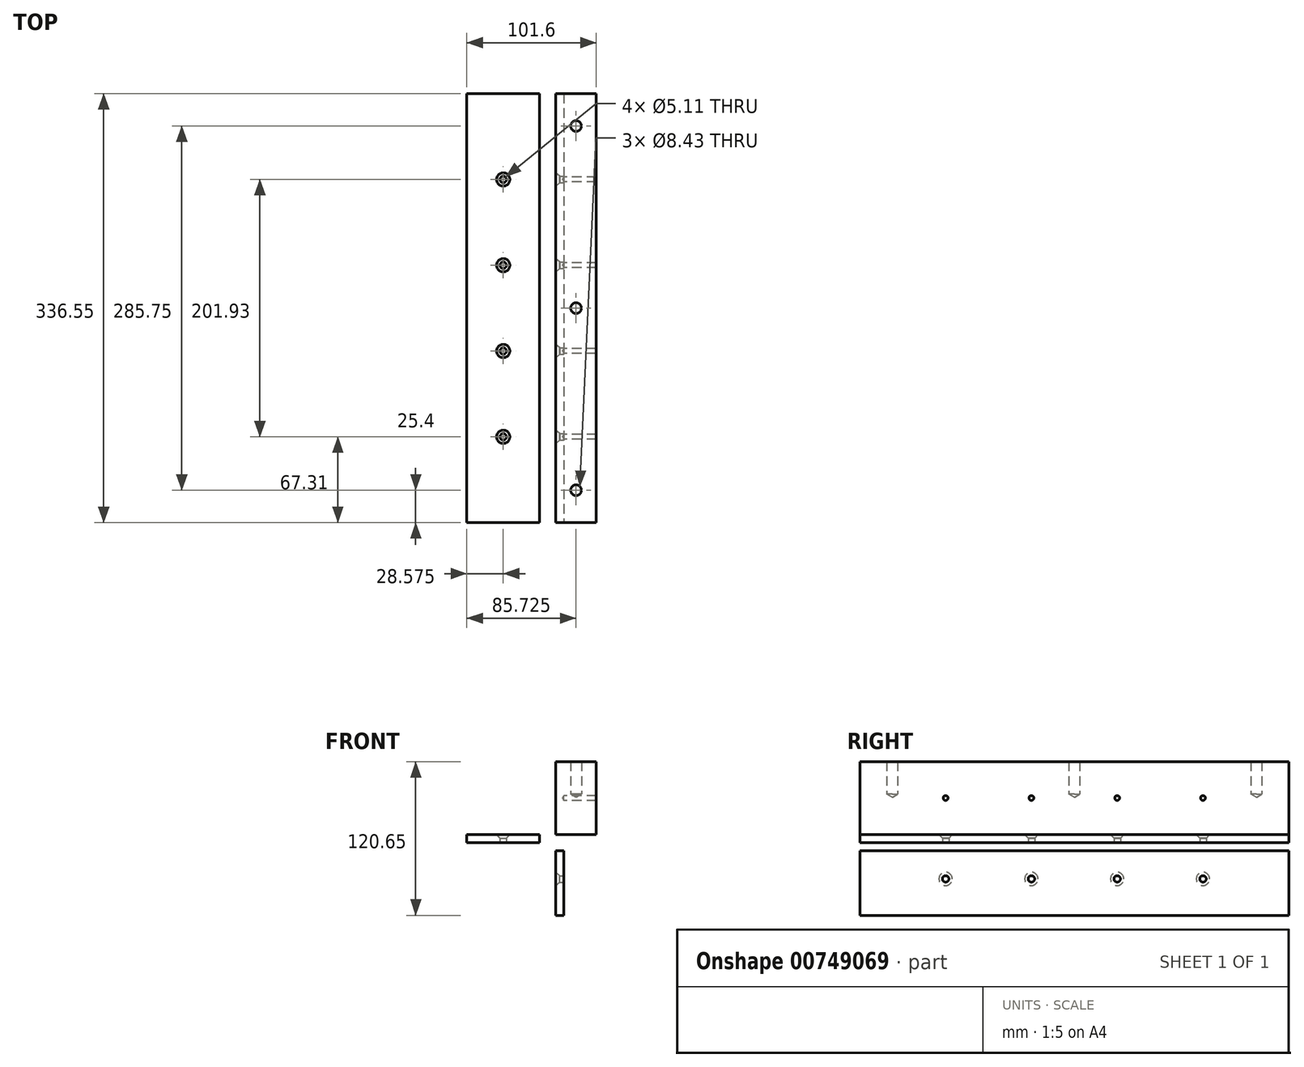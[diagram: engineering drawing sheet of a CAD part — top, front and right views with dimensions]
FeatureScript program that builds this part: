
annotation { "Feature Type Name" : "Feature", "Feature Type Description" : "" }
export const myFeature = defineFeature(function(context is Context, id is Id, definition is map)
    precondition{}
    {
        {
            var Q0;
            Q0=qCreatedBy(makeId("Front.planeOp"),FACE);
            var sketch = newSketch(context, id + "F0", { "sketchPlane" : qUnion([Q0])});
            skLineSegment(sketch, "E0.bottom", {"start": v(0, 0) * mm, "end": v(31.75, 0) * mm});
            skLineSegment(sketch, "E0.top", {"start": v(0, 57.15) * mm, "end": v(31.75, 57.15) * mm});
            skLineSegment(sketch, "E0.left", {"start": v(0, 0) * mm, "end": v(0, 57.15) * mm});
            skLineSegment(sketch, "E0.right", {"start": v(31.75, 0) * mm, "end": v(31.75, 57.15) * mm});
            skSolve(sketch);
        }
        {
            var Q0;
            Q0 = qSketchRegion(id + "F0", true);
            extrude(context, id + "F1", {"entities" : qUnion([Q0]), "depth" : 336.55 * mm, "offsetDistance" : 25.4 * mm});
        }
        {
            var Q0;
            Q0=makeQuery(id+"F1.opExtrude","SWEPT_FACE",FACE,{"disambiguationData":[OSD([sQuery(id+"F0.wireOp",EDGE,"E0.top")])]});
            var sketch = newSketch(context, id + "F2", { "sketchPlane" : qUnion([Q0])});
            skLineSegment(sketch, "E1", {"start": v(15.87, 0) * mm, "end": v(15.87, -336.55) * mm, "construction": true});
            skLineSegment(sketch, "E2", {"start": v(0, -168.28) * mm, "end": v(31.75, -168.28) * mm, "construction": true});
            skPoint(sketch, "E3", {"position": v(15.87, -25.4) * mm});
            skPoint(sketch, "E4", {"position": v(15.87, -168.28) * mm});
            skPoint(sketch, "E5", {"position": v(15.87, -311.15) * mm});
            skSolve(sketch);
        }
        {
            var Q0;
            Q0=sQuery(id+"F2.wireOp",VERTEX,"E3");
            var Q1;
            Q1=sQuery(id+"F2.wireOp",VERTEX,"E4");
            var Q2;
            Q2=sQuery(id+"F2.wireOp",VERTEX,"E5");
            var Q3;
            Q3=makeQuery(id+"F1.opExtrude","SWEPT_BODY",BODY,{"disambiguationData":[OSD([sQuery(id+"F0.wireOp",EDGE,"E0.bottom"),sQuery(id+"F0.wireOp",EDGE,"E0.top"),sQuery(id+"F0.wireOp",EDGE,"E0.left"),sQuery(id+"F0.wireOp",EDGE,"E0.right")])]});
            hole(context, id + "F3", {"style" : HoleStyle.SIMPLE, "endStyle" : HoleEndStyle.BLIND, "standardTappedOrClearance" : lookupTablePath({ "standard" : "ANSI", "engagement" : "75%", "pitch" : "24 tpi", "size" : "3/8", "type" : "Tapped" }), "standardBlindInLast" : lookupTablePath({ "standard" : "ANSI", "engagement" : "75%", "pitch" : "24 tpi", "size" : "3/8", "type" : "Tapped" }), "holeDiameter" : 8.43 * mm, "majorDiameter" : 9.52 * mm, "showTappedDepth" : true, "holeDepth" : 25.4 * mm, "isTappedThrough" : true, "tappedDepth" : 22.22 * mm, "tapClearance" : 3, "locations" : qUnion([Q0, Q1, Q2]), "scope" : qUnion([Q3])});
        }
        {
            var Q0;
            Q0=makeQuery(id+"F1.opExtrude","SWEPT_FACE",FACE,{"disambiguationData":[OSD([sQuery(id+"F0.wireOp",EDGE,"E0.right")])]});
            var sketch = newSketch(context, id + "F4", { "sketchPlane" : qUnion([Q0])});
            skLineSegment(sketch, "E6", {"start": v(0, 28.57) * mm, "end": v(-336.55, 28.57) * mm, "construction": true});
            skPoint(sketch, "E7", {"position": v(-67.31, 28.57) * mm});
            skPoint(sketch, "E8", {"position": v(-134.62, 28.57) * mm});
            skPoint(sketch, "E9", {"position": v(-201.93, 28.57) * mm});
            skPoint(sketch, "E10", {"position": v(-269.24, 28.57) * mm});
            skSolve(sketch);
        }
        {
            var Q0;
            Q0=sQuery(id+"F4.wireOp",VERTEX,"E7");
            var Q1;
            Q1=sQuery(id+"F4.wireOp",VERTEX,"E8");
            var Q2;
            Q2=sQuery(id+"F4.wireOp",VERTEX,"E9");
            var Q3;
            Q3=sQuery(id+"F4.wireOp",VERTEX,"E10");
            var Q4;
            Q4=makeQuery(id+"F1.opExtrude","SWEPT_BODY",BODY,{"disambiguationData":[OSD([sQuery(id+"F0.wireOp",EDGE,"E0.bottom"),sQuery(id+"F0.wireOp",EDGE,"E0.top"),sQuery(id+"F0.wireOp",EDGE,"E0.left"),sQuery(id+"F0.wireOp",EDGE,"E0.right")])]});
            hole(context, id + "F5", {"style" : HoleStyle.SIMPLE, "endStyle" : HoleEndStyle.BLIND, "standardTappedOrClearance" : lookupTablePath({ "standard" : "ANSI", "engagement" : "75%", "pitch" : "24 tpi", "size" : "#10", "type" : "Tapped" }), "standardBlindInLast" : lookupTablePath({ "standard" : "ANSI", "engagement" : "75%", "pitch" : "24 tpi", "size" : "#10", "type" : "Tapped" }), "holeDiameter" : 3.8 * mm, "majorDiameter" : 4.83 * mm, "showTappedDepth" : true, "holeDepth" : 25.4 * mm, "isTappedThrough" : true, "tappedDepth" : 22.22 * mm, "tapClearance" : 3, "locations" : qUnion([Q0, Q1, Q2, Q3]), "scope" : qUnion([Q4])});
        }
        {
            var Q0;
            Q0=qCreatedBy(makeId("Right.planeOp"),FACE);
            var sketch = newSketch(context, id + "F6", { "sketchPlane" : qUnion([Q0])});
            skLineSegment(sketch, "E11.bottom", {"start": v(0, -12.7) * mm, "end": v(-336.55, -12.7) * mm});
            skLineSegment(sketch, "E11.top", {"start": v(0, -63.5) * mm, "end": v(-336.55, -63.5) * mm});
            skLineSegment(sketch, "E11.left", {"start": v(0, -12.7) * mm, "end": v(0, -63.5) * mm});
            skLineSegment(sketch, "E11.right", {"start": v(-336.55, -12.7) * mm, "end": v(-336.55, -63.5) * mm});
            skLineSegment(sketch, "E12", {"start": v(0, -34.93) * mm, "end": v(-336.55, -34.93) * mm, "construction": true});
            skPoint(sketch, "E13", {"position": v(-269.24, -34.93) * mm});
            skPoint(sketch, "E14", {"position": v(-201.93, -34.93) * mm});
            skPoint(sketch, "E15", {"position": v(-134.62, -34.93) * mm});
            skPoint(sketch, "E16", {"position": v(-67.31, -34.93) * mm});
            skSolve(sketch);
        }
        {
            var Q0;
            Q0 = qSketchRegion(id + "F6", true);
            extrude(context, id + "F7", {"entities" : qUnion([Q0]), "depth" : 6.35 * mm, "offsetDistance" : 25.4 * mm});
        }
        {
            var Q0;
            Q0=sQuery(id+"F6.wireOp",VERTEX,"E13");
            var Q1;
            Q1=sQuery(id+"F6.wireOp",VERTEX,"E14");
            var Q2;
            Q2=sQuery(id+"F6.wireOp",VERTEX,"E15");
            var Q3;
            Q3=sQuery(id+"F6.wireOp",VERTEX,"E16");
            var Q4;
            Q4=makeQuery(id+"F7.opExtrude","SWEPT_BODY",BODY,{"disambiguationData":[OSD([sQuery(id+"F6.wireOp",EDGE,"E11.bottom"),sQuery(id+"F6.wireOp",EDGE,"E11.top"),sQuery(id+"F6.wireOp",EDGE,"E11.left"),sQuery(id+"F6.wireOp",EDGE,"E11.right")])]});
            hole(context, id + "F8", {"style" : HoleStyle.C_SINK, "endStyle" : HoleEndStyle.BLIND, "oppositeDirection" : true, "standardTappedOrClearance" : lookupTablePath({ "standard" : "ANSI", "fit" : "Normal (ASME)", "size" : "#10", "type" : "Clearance" }), "standardBlindInLast" : lookupTablePath({ "fit" : "Free", "standard" : "ANSI", "size" : "#10", "type" : "Clearance" }), "holeDiameter" : 5.1 * mm, "cSinkDiameter" : 10.44 * mm, "cSinkAngle" : 82 * degree, "majorDiameter" : 4.83 * mm, "holeDepth" : 25.4 * mm, "isTappedThrough" : true, "tappedDepth" : 22.22 * mm, "tapClearance" : 3, "locations" : qUnion([Q0, Q1, Q2, Q3]), "scope" : qUnion([Q4])});
        }
        {
            var Q0;
            Q0=qCreatedBy(makeId("Top.planeOp"),FACE);
            var sketch = newSketch(context, id + "F9", { "sketchPlane" : qUnion([Q0])});
            skLineSegment(sketch, "E17.bottom", {"start": v(-69.85, 0) * mm, "end": v(-12.7, 0) * mm});
            skLineSegment(sketch, "E17.top", {"start": v(-69.85, -336.55) * mm, "end": v(-12.7, -336.55) * mm});
            skLineSegment(sketch, "E17.left", {"start": v(-69.85, 0) * mm, "end": v(-69.85, -336.55) * mm});
            skLineSegment(sketch, "E17.right", {"start": v(-12.7, 0) * mm, "end": v(-12.7, -336.55) * mm});
            skLineSegment(sketch, "E18", {"start": v(-41.28, 0) * mm, "end": v(-41.27, -336.55) * mm, "construction": true});
            skPoint(sketch, "E19", {"position": v(-41.28, -67.31) * mm});
            skPoint(sketch, "E20", {"position": v(-41.28, -134.62) * mm});
            skPoint(sketch, "E21", {"position": v(-41.28, -201.93) * mm});
            skPoint(sketch, "E22", {"position": v(-41.27, -269.24) * mm});
            skSolve(sketch);
        }
        {
            var Q0;
            Q0 = qSketchRegion(id + "F9", true);
            extrude(context, id + "F10", {"entities" : qUnion([Q0]), "oppositeDirection" : true, "depth" : 6.35 * mm, "offsetDistance" : 25.4 * mm});
        }
        {
            var Q0;
            Q0=sQuery(id+"F9.wireOp",VERTEX,"E19");
            var Q1;
            Q1=sQuery(id+"F9.wireOp",VERTEX,"E20");
            var Q2;
            Q2=sQuery(id+"F9.wireOp",VERTEX,"E21");
            var Q3;
            Q3=sQuery(id+"F9.wireOp",VERTEX,"E22");
            var Q4;
            Q4=makeQuery(id+"F10.opExtrude","SWEPT_BODY",BODY,{"disambiguationData":[OSD([sQuery(id+"F9.wireOp",EDGE,"E17.bottom"),sQuery(id+"F9.wireOp",EDGE,"E17.top"),sQuery(id+"F9.wireOp",EDGE,"E17.left"),sQuery(id+"F9.wireOp",EDGE,"E17.right")])]});
            hole(context, id + "F11", {"style" : HoleStyle.C_SINK, "endStyle" : HoleEndStyle.BLIND, "standardTappedOrClearance" : lookupTablePath({ "standard" : "ANSI", "fit" : "Normal (ASME)", "size" : "#10", "type" : "Clearance" }), "standardBlindInLast" : lookupTablePath({ "fit" : "Free", "standard" : "ANSI", "size" : "#10", "type" : "Clearance" }), "holeDiameter" : 5.1 * mm, "cSinkDiameter" : 10.44 * mm, "cSinkAngle" : 82 * degree, "majorDiameter" : 4.83 * mm, "holeDepth" : 25.4 * mm, "isTappedThrough" : true, "tappedDepth" : 22.22 * mm, "tapClearance" : 3, "locations" : qUnion([Q0, Q1, Q2, Q3]), "scope" : qUnion([Q4])});
        }
    });
